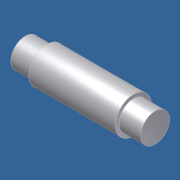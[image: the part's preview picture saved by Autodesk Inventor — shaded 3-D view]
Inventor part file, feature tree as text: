
AUTODESK INVENTOR PART (.ipt)
format: ipt  version: unknown  size: 172,544 bytes
history: native  units: in
note: dims shown in document units (in); Inventor stores cm internally (conversion verified against a paired STEP export)
features: revolve x1, sketch x1
ambient origin geometry x8: Origin, YZ Plane, XZ Plane, XY Plane, X Axis, Y Axis, Z Axis, Center Point
bodies: Solid1 (feature_tree)
feature tree (2):
  revolve  "Revolution1"  [1 undecoded]
  sketch  "Sketch1"  dims[d0=0.1875in d1=0.1875in d2=0.125in d3=0.125in d4=0.75in d5=0.1562in d6=90.0deg]
note: 1 required parameter value undecoded (feature->parameter linkage not recoverable at this tier; creation-order binding heuristic only, values carry confidence <= 0.55)
